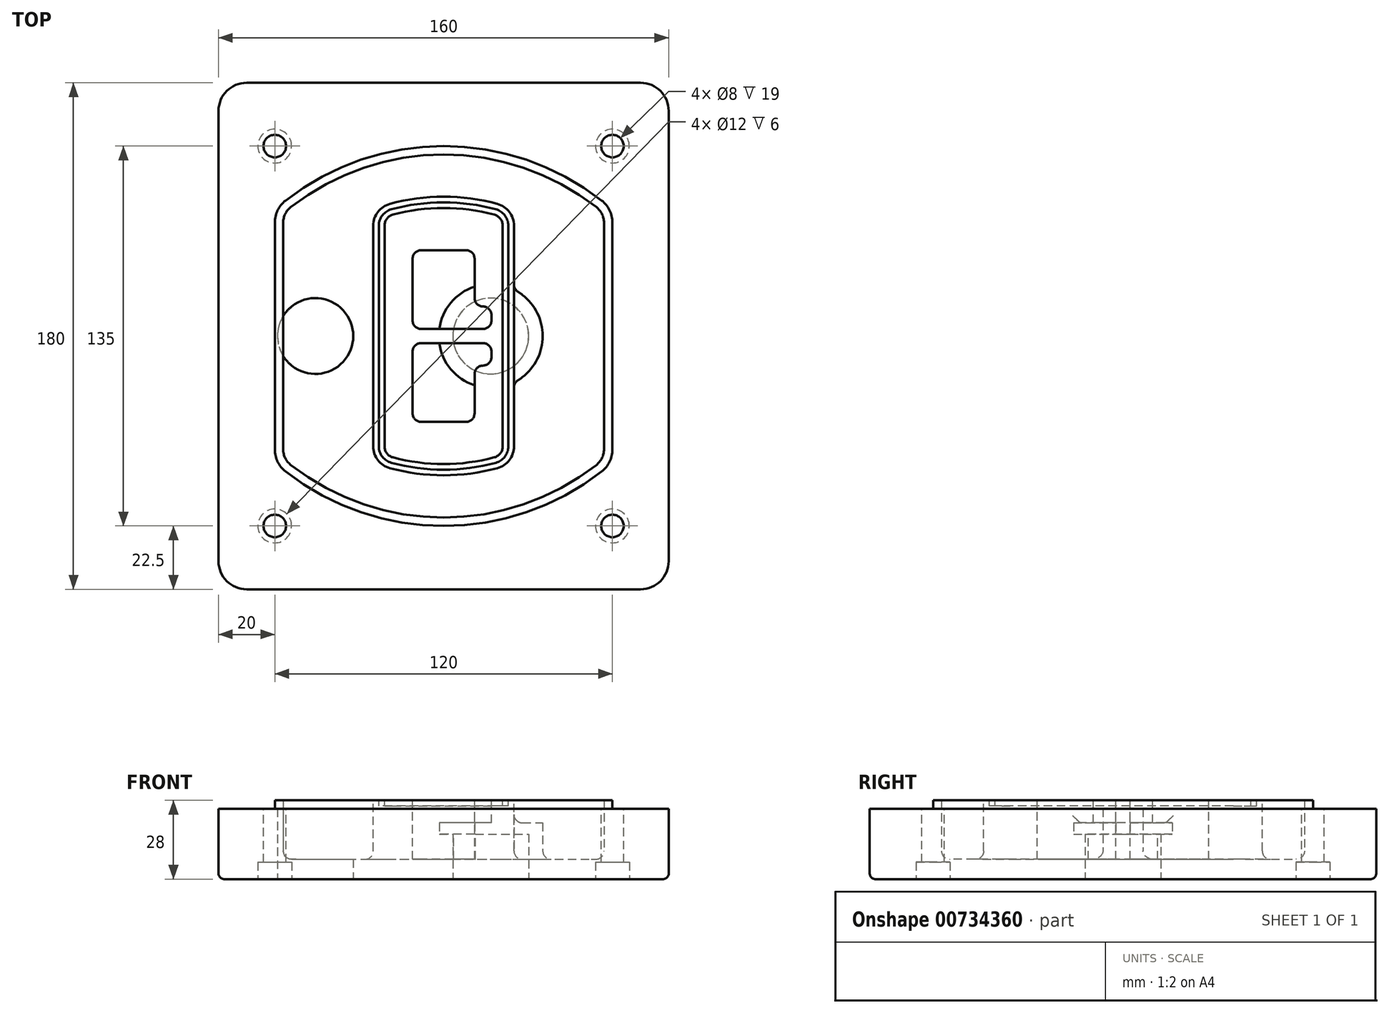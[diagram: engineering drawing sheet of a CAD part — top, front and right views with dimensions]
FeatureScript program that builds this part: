
annotation { "Feature Type Name" : "Feature", "Feature Type Description" : "" }
export const myFeature = defineFeature(function(context is Context, id is Id, definition is map)
    precondition{}
    {
        {
            var Q0;
            Q0=qCreatedBy(makeId("Top.planeOp"),FACE);
            var sketch = newSketch(context, id + "F0", { "sketchPlane" : qUnion([Q0])});
            skPoint(sketch, "E0.rect.middle", {"position": v(0, 0) * mm});
            skLineSegment(sketch, "E1.bottom", {"start": v(-70, -90) * mm, "end": v(70, -90) * mm});
            skLineSegment(sketch, "E1.top", {"start": v(-70, 90) * mm, "end": v(70, 90) * mm});
            skLineSegment(sketch, "E1.left", {"start": v(-80, -80) * mm, "end": v(-80, 80) * mm});
            skLineSegment(sketch, "E1.right", {"start": v(80, -80) * mm, "end": v(80, 80) * mm});
            skLineSegment(sketch, "E2", {"start": v(-80, 90) * mm, "end": v(80, -90) * mm, "construction": true});
            skLineSegment(sketch, "E3", {"start": v(80, 90) * mm, "end": v(-80, -90) * mm, "construction": true});
            skCircle(sketch, "E4", {"center": v(-60, 67.5) * mm, "radius": 4 * mm});
            skCircle(sketch, "E5", {"center": v(60, 67.5) * mm, "radius": 4 * mm});
            skCircle(sketch, "E6", {"center": v(60, -67.5) * mm, "radius": 4 * mm});
            skCircle(sketch, "E7", {"center": v(-60, -67.5) * mm, "radius": 4 * mm});
            skLineSegment(sketch, "E8", {"start": v(-60, 67.5) * mm, "end": v(60, 67.5) * mm, "construction": true});
            skLineSegment(sketch, "E9", {"start": v(60, 67.5) * mm, "end": v(60, -67.5) * mm, "construction": true});
            skLineSegment(sketch, "E10", {"start": v(60, -67.5) * mm, "end": v(-60, -67.5) * mm, "construction": true});
            skLineSegment(sketch, "E11", {"start": v(-60, -67.5) * mm, "end": v(-60, 67.5) * mm, "construction": true});
            skLineSegment(sketch, "E12", {"start": v(-60, 40.3) * mm, "end": v(-60, -40.3) * mm});
            skLineSegment(sketch, "E13", {"start": v(60, 40.3) * mm, "end": v(60, -40.3) * mm});
            skArc(sketch, "E14", {"start": v(56.15, 48.18) * mm, "mid": v(0, 67.5) * mm, "end": v(-56.15, 48.18) * mm});
            skArc(sketch, "E15", {"start": v(-56.15, -48.18) * mm, "mid": v(0, -67.5) * mm, "end": v(56.15, -48.18) * mm});
            skLineSegment(sketch, "E16", {"start": v(-60, 0) * mm, "end": v(60, 0) * mm, "construction": true});
            skPoint(sketch, "E17.visualSharp", {"position": v(-60, -45) * mm});
            skArc(sketch, "E17.filletArc", {"start": v(-60, -40.3) * mm, "mid": v(-58.99, -44.68) * mm, "end": v(-56.15, -48.18) * mm});
            skPoint(sketch, "E18.visualSharp", {"position": v(-60, 45) * mm});
            skArc(sketch, "E18.filletArc", {"start": v(-56.15, 48.18) * mm, "mid": v(-58.99, 44.68) * mm, "end": v(-60, 40.3) * mm});
            skPoint(sketch, "E19.visualSharp", {"position": v(60, 45) * mm});
            skArc(sketch, "E19.filletArc", {"start": v(60, 40.3) * mm, "mid": v(58.99, 44.68) * mm, "end": v(56.15, 48.18) * mm});
            skPoint(sketch, "E20.visualSharp", {"position": v(60, -45) * mm});
            skArc(sketch, "E20.filletArc", {"start": v(56.15, -48.18) * mm, "mid": v(58.99, -44.68) * mm, "end": v(60, -40.3) * mm});
            skPoint(sketch, "E21.visualSharp", {"position": v(-80, 90) * mm});
            skArc(sketch, "E21.filletArc", {"start": v(-70, 90) * mm, "mid": v(-77.07, 87.07) * mm, "end": v(-80, 80) * mm});
            skPoint(sketch, "E22.visualSharp", {"position": v(80, 90) * mm});
            skArc(sketch, "E22.filletArc", {"start": v(80, 80) * mm, "mid": v(77.07, 87.07) * mm, "end": v(70, 90) * mm});
            skPoint(sketch, "E23.visualSharp", {"position": v(80, -90) * mm});
            skArc(sketch, "E23.filletArc", {"start": v(70, -90) * mm, "mid": v(77.07, -87.07) * mm, "end": v(80, -80) * mm});
            skPoint(sketch, "E24.visualSharp", {"position": v(-80, -90) * mm});
            skArc(sketch, "E24.filletArc", {"start": v(-80, -80) * mm, "mid": v(-77.07, -87.07) * mm, "end": v(-70, -90) * mm});
            skArc(sketch, "E25.0", {"start": v(57, 40.3) * mm, "mid": v(56.3, 43.36) * mm, "end": v(54.3, 45.81) * mm});
            skLineSegment(sketch, "E25.1", {"start": v(57, 40.3) * mm, "end": v(57, -40.3) * mm});
            skArc(sketch, "E25.2", {"start": v(54.3, -45.81) * mm, "mid": v(56.3, -43.36) * mm, "end": v(57, -40.3) * mm});
            skArc(sketch, "E25.3", {"start": v(-54.3, -45.81) * mm, "mid": v(0, -64.5) * mm, "end": v(54.3, -45.81) * mm});
            skArc(sketch, "E25.4", {"start": v(-57, -40.3) * mm, "mid": v(-56.3, -43.36) * mm, "end": v(-54.3, -45.81) * mm});
            skArc(sketch, "E25.5", {"start": v(54.3, 45.81) * mm, "mid": v(0, 64.5) * mm, "end": v(-54.3, 45.81) * mm});
            skLineSegment(sketch, "E25.6", {"start": v(-57, 40.3) * mm, "end": v(-57, -40.3) * mm});
            skArc(sketch, "E25.7", {"start": v(-54.3, 45.81) * mm, "mid": v(-56.3, 43.36) * mm, "end": v(-57, 40.3) * mm});
            skArc(sketch, "E26.0", {"start": v(-58.62, 51.33) * mm, "mid": v(-62.58, 46.43) * mm, "end": v(-64, 40.3) * mm});
            skArc(sketch, "E26.1", {"start": v(58.62, 51.33) * mm, "mid": v(0, 71.5) * mm, "end": v(-58.62, 51.33) * mm});
            skArc(sketch, "E26.2", {"start": v(64, 40.3) * mm, "mid": v(62.58, 46.43) * mm, "end": v(58.62, 51.33) * mm});
            skLineSegment(sketch, "E26.3", {"start": v(64, 40.3) * mm, "end": v(64, -40.3) * mm});
            skArc(sketch, "E26.4", {"start": v(58.62, -51.33) * mm, "mid": v(62.58, -46.43) * mm, "end": v(64, -40.3) * mm});
            skLineSegment(sketch, "E26.5", {"start": v(-64, 40.3) * mm, "end": v(-64, -40.3) * mm});
            skArc(sketch, "E26.6", {"start": v(-58.62, -51.33) * mm, "mid": v(0, -71.5) * mm, "end": v(58.62, -51.33) * mm});
            skArc(sketch, "E26.7", {"start": v(-64, -40.3) * mm, "mid": v(-62.58, -46.43) * mm, "end": v(-58.62, -51.33) * mm});
            skSolve(sketch);
        }
        {
            var Q0;
            Q0=makeQuery(id+"F0.imprint","IMPRINT",FACE,{"disambiguationData":[TD([[makeQuery(id+"F0.imprint","IMPRINT",EDGE,{"derivedFrom":sQuery(id+"F0.wireOp",EDGE,"E1.bottom")}),1.0]])]});
            var Q1;
            Q1=makeQuery(id+"F0.imprint","IMPRINT",FACE,{"disambiguationData":[TD([[makeQuery(id+"F0.imprint","IMPRINT",EDGE,{"derivedFrom":sQuery(id+"F0.wireOp",EDGE,"E12")}),1.0]])]});
            var Q2;
            Q2=makeQuery(id+"F0.imprint","IMPRINT",FACE,{"disambiguationData":[TD([[makeQuery(id+"F0.imprint","IMPRINT",EDGE,{"derivedFrom":sQuery(id+"F0.wireOp",EDGE,"E25.0")}),1.0]])]});
            var Q3;
            Q3=makeQuery(id+"F0.imprint","IMPRINT",FACE,{"disambiguationData":[TD([[makeQuery(id+"F0.imprint","IMPRINT",EDGE,{"derivedFrom":sQuery(id+"F0.wireOp",EDGE,"E12")}),-1.0]])]});
            extrude(context, id + "F1", {"entities" : qUnion([Q0, Q1, Q2, Q3]), "oppositeDirection" : true, "depth" : 25 * mm, "offsetDistance" : 25 * mm});
        }
        {
            var Q0;
            Q0=makeQuery(id+"F0.imprint","IMPRINT",FACE,{"disambiguationData":[TD([[makeQuery(id+"F0.imprint","IMPRINT",EDGE,{"derivedFrom":sQuery(id+"F0.wireOp",EDGE,"E12")}),1.0]])]});
            extrude(context, id + "F2", {"entities" : qUnion([Q0]), "operationType" : NewBodyOperationType.ADD, "depth" : 3 * mm, "offsetDistance" : 25 * mm});
        }
        {
            var Q0;
            Q0=makeQuery(id+"F0.imprint","IMPRINT",FACE,{"disambiguationData":[TD([[makeQuery(id+"F0.imprint","IMPRINT",EDGE,{"derivedFrom":sQuery(id+"F0.wireOp",EDGE,"E25.0")}),1.0]])]});
            extrude(context, id + "F3", {"entities" : qUnion([Q0]), "operationType" : NewBodyOperationType.REMOVE, "oppositeDirection" : true, "depth" : 18 * mm, "offsetDistance" : 25 * mm});
        }
        {
            var Q0;
            Q0=makeQuery(id+"F2.opExtrude","CAP_FACE",FACE,{"disambiguationData":[OSD([sQuery(id+"F0.wireOp",EDGE,"E12"),sQuery(id+"F0.wireOp",EDGE,"E13"),sQuery(id+"F0.wireOp",EDGE,"E14"),sQuery(id+"F0.wireOp",EDGE,"E15"),sQuery(id+"F0.wireOp",EDGE,"E17.filletArc"),sQuery(id+"F0.wireOp",EDGE,"E18.filletArc"),sQuery(id+"F0.wireOp",EDGE,"E19.filletArc"),sQuery(id+"F0.wireOp",EDGE,"E20.filletArc"),sQuery(id+"F0.wireOp",EDGE,"E25.0"),sQuery(id+"F0.wireOp",EDGE,"E25.1"),sQuery(id+"F0.wireOp",EDGE,"E25.2"),sQuery(id+"F0.wireOp",EDGE,"E25.3"),sQuery(id+"F0.wireOp",EDGE,"E25.4"),sQuery(id+"F0.wireOp",EDGE,"E25.5"),sQuery(id+"F0.wireOp",EDGE,"E25.6"),sQuery(id+"F0.wireOp",EDGE,"E25.7")])],"isStart":false});
            var sketch = newSketch(context, id + "F4", { "sketchPlane" : qUnion([Q0])});
            skArc(sketch, "E27.0", {"start": v(-19.08, -46.97) * mm, "mid": v(0, -49.5) * mm, "end": v(19.08, -46.97) * mm});
            skArc(sketch, "E28.0", {"start": v(19.08, 46.97) * mm, "mid": v(0, 49.5) * mm, "end": v(-19.08, 46.97) * mm});
            skLineSegment(sketch, "E29", {"start": v(-25, 39.25) * mm, "end": v(-25, -39.25) * mm});
            skLineSegment(sketch, "E30", {"start": v(25, 39.25) * mm, "end": v(25, -39.25) * mm});
            skLineSegment(sketch, "E31", {"start": v(-25, 45.1) * mm, "end": v(25, 45.1) * mm, "construction": true});
            skLineSegment(sketch, "E32", {"start": v(-25, -45.1) * mm, "end": v(25, -45.1) * mm, "construction": true});
            skPoint(sketch, "E33.visualSharp", {"position": v(-25, 45.1) * mm});
            skArc(sketch, "E33.filletArc", {"start": v(-19.08, 46.97) * mm, "mid": v(-23.35, 44.11) * mm, "end": v(-25, 39.25) * mm});
            skPoint(sketch, "E34.visualSharp", {"position": v(25, 45.1) * mm});
            skArc(sketch, "E34.filletArc", {"start": v(25, 39.25) * mm, "mid": v(23.35, 44.11) * mm, "end": v(19.08, 46.97) * mm});
            skPoint(sketch, "E35.visualSharp", {"position": v(25, -45.1) * mm});
            skArc(sketch, "E35.filletArc", {"start": v(19.08, -46.97) * mm, "mid": v(23.35, -44.11) * mm, "end": v(25, -39.25) * mm});
            skPoint(sketch, "E36.visualSharp", {"position": v(-25, -45.1) * mm});
            skArc(sketch, "E36.filletArc", {"start": v(-25, -39.25) * mm, "mid": v(-23.35, -44.11) * mm, "end": v(-19.08, -46.97) * mm});
            skArc(sketch, "E37.0", {"start": v(54.3, 45.81) * mm, "mid": v(0, 64.5) * mm, "end": v(-54.3, 45.81) * mm});
            skArc(sketch, "E37.1", {"start": v(-54.3, 45.81) * mm, "mid": v(-56.3, 43.36) * mm, "end": v(-57, 40.3) * mm});
            skLineSegment(sketch, "E37.2", {"start": v(-57, 40.3) * mm, "end": v(-57, -40.3) * mm});
            skArc(sketch, "E37.3", {"start": v(-57, -40.3) * mm, "mid": v(-56.3, -43.36) * mm, "end": v(-54.3, -45.81) * mm});
            skArc(sketch, "E37.4", {"start": v(-54.3, -45.81) * mm, "mid": v(0, -64.5) * mm, "end": v(54.3, -45.81) * mm});
            skArc(sketch, "E37.5", {"start": v(54.3, -45.81) * mm, "mid": v(56.3, -43.36) * mm, "end": v(57, -40.3) * mm});
            skLineSegment(sketch, "E37.6", {"start": v(57, 40.3) * mm, "end": v(57, -40.3) * mm});
            skArc(sketch, "E37.7", {"start": v(57, 40.3) * mm, "mid": v(56.3, 43.36) * mm, "end": v(54.3, 45.81) * mm});
            skLineSegment(sketch, "E38.0", {"start": v(23, 39.25) * mm, "end": v(23, -39.25) * mm});
            skArc(sketch, "E38.1", {"start": v(18.56, -45.04) * mm, "mid": v(21.76, -42.9) * mm, "end": v(23, -39.25) * mm});
            skArc(sketch, "E38.2", {"start": v(-18.56, -45.04) * mm, "mid": v(0, -47.5) * mm, "end": v(18.56, -45.04) * mm});
            skArc(sketch, "E38.3", {"start": v(-23, -39.25) * mm, "mid": v(-21.76, -42.9) * mm, "end": v(-18.56, -45.04) * mm});
            skLineSegment(sketch, "E38.4", {"start": v(-23, 39.25) * mm, "end": v(-23, -39.25) * mm});
            skArc(sketch, "E38.5", {"start": v(23, 39.25) * mm, "mid": v(21.76, 42.9) * mm, "end": v(18.56, 45.04) * mm});
            skArc(sketch, "E38.6", {"start": v(-18.56, 45.04) * mm, "mid": v(-21.76, 42.9) * mm, "end": v(-23, 39.25) * mm});
            skArc(sketch, "E38.7", {"start": v(18.56, 45.04) * mm, "mid": v(0, 47.5) * mm, "end": v(-18.56, 45.04) * mm});
            skArc(sketch, "E39.0", {"start": v(21, 39.25) * mm, "mid": v(20.18, 41.68) * mm, "end": v(18.04, 43.1) * mm});
            skLineSegment(sketch, "E39.1", {"start": v(21, 39.25) * mm, "end": v(21, -39.25) * mm});
            skArc(sketch, "E39.2", {"start": v(18.04, -43.1) * mm, "mid": v(20.18, -41.68) * mm, "end": v(21, -39.25) * mm});
            skArc(sketch, "E39.3", {"start": v(-18.04, -43.1) * mm, "mid": v(0, -45.5) * mm, "end": v(18.04, -43.1) * mm});
            skArc(sketch, "E39.4", {"start": v(-21, -39.25) * mm, "mid": v(-20.18, -41.68) * mm, "end": v(-18.04, -43.1) * mm});
            skArc(sketch, "E39.5", {"start": v(18.04, 43.1) * mm, "mid": v(0, 45.5) * mm, "end": v(-18.04, 43.1) * mm});
            skLineSegment(sketch, "E39.6", {"start": v(-21, 39.25) * mm, "end": v(-21, -39.25) * mm});
            skArc(sketch, "E39.7", {"start": v(-18.04, 43.1) * mm, "mid": v(-20.18, 41.68) * mm, "end": v(-21, 39.25) * mm});
            skLineSegment(sketch, "E40", {"start": v(-25, 0) * mm, "end": v(25, 0) * mm, "construction": true});
            skLineSegment(sketch, "E41", {"start": v(-11, 5.5) * mm, "end": v(-11, 27.5) * mm});
            skLineSegment(sketch, "E42", {"start": v(-8, 30.5) * mm, "end": v(8, 30.5) * mm});
            skLineSegment(sketch, "E43", {"start": v(11, 27.5) * mm, "end": v(11, 13.5) * mm});
            skLineSegment(sketch, "E44", {"start": v(14, 10.5) * mm, "end": v(14, 10.5) * mm});
            skLineSegment(sketch, "E45", {"start": v(17, 7.5) * mm, "end": v(17, 5.5) * mm});
            skLineSegment(sketch, "E46", {"start": v(14, 2.5) * mm, "end": v(-8, 2.5) * mm});
            skPoint(sketch, "E47.visualSharp", {"position": v(-11, 30.5) * mm});
            skArc(sketch, "E47.filletArc", {"start": v(-8, 30.5) * mm, "mid": v(-10.12, 29.62) * mm, "end": v(-11, 27.5) * mm});
            skPoint(sketch, "E48.visualSharp", {"position": v(11, 30.5) * mm});
            skArc(sketch, "E48.filletArc", {"start": v(11, 27.5) * mm, "mid": v(10.12, 29.62) * mm, "end": v(8, 30.5) * mm});
            skPoint(sketch, "E49.visualSharp", {"position": v(11, 10.5) * mm});
            skArc(sketch, "E49.filletArc", {"start": v(11, 13.5) * mm, "mid": v(11.88, 11.38) * mm, "end": v(14, 10.5) * mm});
            skPoint(sketch, "E50.visualSharp", {"position": v(17, 10.5) * mm});
            skArc(sketch, "E50.filletArc", {"start": v(17, 7.5) * mm, "mid": v(16.12, 9.62) * mm, "end": v(14, 10.5) * mm});
            skPoint(sketch, "E51.visualSharp", {"position": v(17, 2.5) * mm});
            skArc(sketch, "E51.filletArc", {"start": v(14, 2.5) * mm, "mid": v(16.12, 3.38) * mm, "end": v(17, 5.5) * mm});
            skPoint(sketch, "E52.visualSharp", {"position": v(-11, 2.5) * mm});
            skArc(sketch, "E52.filletArc", {"start": v(-11, 5.5) * mm, "mid": v(-10.12, 3.38) * mm, "end": v(-8, 2.5) * mm});
            skLineSegment(sketch, "E53.0.MirrorCS", {"start": v(14, -2.5) * mm, "end": v(-8, -2.5) * mm});
            skArc(sketch, "E54.0.MirrorCS", {"start": v(-11, -5.5) * mm, "mid": v(-10.12, -3.38) * mm, "end": v(-8, -2.5) * mm});
            skLineSegment(sketch, "E55.0.MirrorCS", {"start": v(-11, -5.5) * mm, "end": v(-11, -27.5) * mm});
            skArc(sketch, "E56.0.MirrorCS", {"start": v(-8, -30.5) * mm, "mid": v(-10.12, -29.62) * mm, "end": v(-11, -27.5) * mm});
            skLineSegment(sketch, "E57.0.MirrorCS", {"start": v(-8, -30.5) * mm, "end": v(8, -30.5) * mm});
            skArc(sketch, "E58.0.MirrorCS", {"start": v(11, -27.5) * mm, "mid": v(10.12, -29.62) * mm, "end": v(8, -30.5) * mm});
            skLineSegment(sketch, "E59.0.MirrorCS", {"start": v(11, -27.5) * mm, "end": v(11, -13.5) * mm});
            skArc(sketch, "E60.0.MirrorCS", {"start": v(11, -13.5) * mm, "mid": v(11.88, -11.38) * mm, "end": v(14, -10.5) * mm});
            skArc(sketch, "E61.0.MirrorCS", {"start": v(17, -7.5) * mm, "mid": v(16.12, -9.62) * mm, "end": v(14, -10.5) * mm});
            skLineSegment(sketch, "E62.0.MirrorCS", {"start": v(17, -7.5) * mm, "end": v(17, -5.5) * mm});
            skArc(sketch, "E63.0.MirrorCS", {"start": v(14, -2.5) * mm, "mid": v(16.12, -3.38) * mm, "end": v(17, -5.5) * mm});
            skSolve(sketch);
        }
        {
            var Q0;
            Q0=makeQuery(id+"F4.imprint","IMPRINT",FACE,{"disambiguationData":[TD([[makeQuery(id+"F4.imprint","IMPRINT",EDGE,{"derivedFrom":sQuery(id+"F4.wireOp",EDGE,"E27.0")}),1.0]])]});
            var Q1;
            Q1=makeQuery(id+"F4.imprint","IMPRINT",FACE,{"disambiguationData":[TD([[makeQuery(id+"F4.imprint","IMPRINT",EDGE,{"derivedFrom":sQuery(id+"F4.wireOp",EDGE,"E38.0")}),-1.0]])]});
            var Q2;
            Q2=makeQuery(id+"F4.imprint","IMPRINT",FACE,{"disambiguationData":[TD([[makeQuery(id+"F4.imprint","IMPRINT",EDGE,{"derivedFrom":sQuery(id+"F4.wireOp",EDGE,"E39.0")}),1.0]])]});
            extrude(context, id + "F5", {"entities" : qUnion([Q0, Q1, Q2]), "operationType" : NewBodyOperationType.ADD, "endBound" : BoundingType.UP_TO_NEXT, "oppositeDirection" : true, "depth" : 25 * mm});
        }
        {
            var Q0;
            Q0=makeQuery(id+"F4.imprint","IMPRINT",FACE,{"disambiguationData":[TD([[makeQuery(id+"F4.imprint","IMPRINT",EDGE,{"derivedFrom":sQuery(id+"F4.wireOp",EDGE,"E38.0")}),-1.0]])]});
            extrude(context, id + "F6", {"entities" : qUnion([Q0]), "operationType" : NewBodyOperationType.REMOVE, "oppositeDirection" : true, "depth" : 2 * mm});
        }
        {
            var Q0;
            Q0=makeQuery(id+"F1.opExtrude","CAP_FACE",FACE,{"disambiguationData":[OSD([sQuery(id+"F0.wireOp",EDGE,"E1.bottom"),sQuery(id+"F0.wireOp",EDGE,"E1.top"),sQuery(id+"F0.wireOp",EDGE,"E1.left"),sQuery(id+"F0.wireOp",EDGE,"E1.right"),sQuery(id+"F0.wireOp",EDGE,"E4"),sQuery(id+"F0.wireOp",EDGE,"E5"),sQuery(id+"F0.wireOp",EDGE,"E6"),sQuery(id+"F0.wireOp",EDGE,"E7"),sQuery(id+"F0.wireOp",EDGE,"E21.filletArc"),sQuery(id+"F0.wireOp",EDGE,"E22.filletArc"),sQuery(id+"F0.wireOp",EDGE,"E23.filletArc"),sQuery(id+"F0.wireOp",EDGE,"E24.filletArc")])],"isStart":false});
            var sketch = newSketch(context, id + "F7", { "sketchPlane" : qUnion([Q0])});
            skCircle(sketch, "E64", {"center": v(16.76, 0) * mm, "radius": 13.47 * mm});
            skCircle(sketch, "E65", {"center": v(-45.56, 0) * mm, "radius": 13.47 * mm});
            skLineSegment(sketch, "E66", {"start": v(80, 0) * mm, "end": v(-80, 0) * mm});
            skCircle(sketch, "E67", {"center": v(16.76, 0) * mm, "radius": 18.47 * mm});
            skCircle(sketch, "E68", {"center": v(60, -67.5) * mm, "radius": 6 * mm});
            skCircle(sketch, "E69", {"center": v(-60, -67.5) * mm, "radius": 6 * mm});
            skCircle(sketch, "E70", {"center": v(-60, 67.5) * mm, "radius": 6 * mm});
            skCircle(sketch, "E71", {"center": v(60, 67.5) * mm, "radius": 6 * mm});
            skSolve(sketch);
        }
        {
            var Q0;
            {var subQ1=sQuery(id+"F7.wireOp",EDGE,"E66");var subQ4=sQuery(id+"F7.wireOp",EDGE,"E64");var subQ6=makeQuery(id+"F7.imprint","INTERSECT",VERTEX,{"disambiguationData":[OD(0.0)],"derivedFrom":[subQ4,subQ1]});Q0=makeQuery(id+"F7.imprint","IMPRINT",FACE,{"disambiguationData":[TD([[makeQuery(id+"F7.imprint","IMPRINT",EDGE,{"disambiguationData":[TD([[subQ6,-1.0]])],"derivedFrom":subQ4}),-1.0]])]});}
            var Q1;
            {var subQ0=sQuery(id+"F7.wireOp",EDGE,"E66");var subQ1=sQuery(id+"F7.wireOp",EDGE,"E64");var subQ3=makeQuery(id+"F7.imprint","INTERSECT",VERTEX,{"disambiguationData":[OD(0.0)],"derivedFrom":[subQ1,subQ0]});Q1=makeQuery(id+"F7.imprint","IMPRINT",FACE,{"disambiguationData":[TD([[makeQuery(id+"F7.imprint","IMPRINT",EDGE,{"disambiguationData":[TD([[subQ3,-1.0]])],"derivedFrom":subQ1}),1.0]])]});}
            var Q2;
            {var subQ0=sQuery(id+"F7.wireOp",EDGE,"E66");var subQ1=sQuery(id+"F7.wireOp",EDGE,"E64");var subQ3=makeQuery(id+"F7.imprint","INTERSECT",VERTEX,{"disambiguationData":[OD(0.0)],"derivedFrom":[subQ1,subQ0]});Q2=makeQuery(id+"F7.imprint","IMPRINT",FACE,{"disambiguationData":[TD([[makeQuery(id+"F7.imprint","IMPRINT",EDGE,{"disambiguationData":[TD([[subQ3,1.0]])],"derivedFrom":subQ1}),1.0]])]});}
            var Q3;
            {var subQ1=sQuery(id+"F7.wireOp",EDGE,"E66");var subQ4=sQuery(id+"F7.wireOp",EDGE,"E64");var subQ6=makeQuery(id+"F7.imprint","INTERSECT",VERTEX,{"disambiguationData":[OD(0.0)],"derivedFrom":[subQ4,subQ1]});Q3=makeQuery(id+"F7.imprint","IMPRINT",FACE,{"disambiguationData":[TD([[makeQuery(id+"F7.imprint","IMPRINT",EDGE,{"disambiguationData":[TD([[subQ6,1.0]])],"derivedFrom":subQ4}),-1.0]])]});}
            extrude(context, id + "F8", {"entities" : qUnion([Q0, Q1, Q2, Q3]), "operationType" : NewBodyOperationType.ADD, "oppositeDirection" : true, "depth" : 20 * mm});
        }
        {
            var Q0;
            {var subQ0=sQuery(id+"F7.wireOp",EDGE,"E66");var subQ1=sQuery(id+"F7.wireOp",EDGE,"E64");var subQ3=makeQuery(id+"F7.imprint","INTERSECT",VERTEX,{"disambiguationData":[OD(0.0)],"derivedFrom":[subQ1,subQ0]});Q0=makeQuery(id+"F7.imprint","IMPRINT",FACE,{"disambiguationData":[TD([[makeQuery(id+"F7.imprint","IMPRINT",EDGE,{"disambiguationData":[TD([[subQ3,-1.0]])],"derivedFrom":subQ1}),1.0]])]});}
            var Q1;
            {var subQ0=sQuery(id+"F7.wireOp",EDGE,"E66");var subQ1=sQuery(id+"F7.wireOp",EDGE,"E64");var subQ3=makeQuery(id+"F7.imprint","INTERSECT",VERTEX,{"disambiguationData":[OD(0.0)],"derivedFrom":[subQ1,subQ0]});Q1=makeQuery(id+"F7.imprint","IMPRINT",FACE,{"disambiguationData":[TD([[makeQuery(id+"F7.imprint","IMPRINT",EDGE,{"disambiguationData":[TD([[subQ3,1.0]])],"derivedFrom":subQ1}),1.0]])]});}
            extrude(context, id + "F9", {"entities" : qUnion([Q0, Q1]), "operationType" : NewBodyOperationType.REMOVE, "oppositeDirection" : true, "depth" : 16 * mm});
        }
        {
            var Q0;
            {var subQ0=sQuery(id+"F7.wireOp",EDGE,"E66");var subQ1=sQuery(id+"F7.wireOp",EDGE,"E65");var subQ3=makeQuery(id+"F7.imprint","INTERSECT",VERTEX,{"disambiguationData":[OD(0.0)],"derivedFrom":[subQ1,subQ0]});Q0=makeQuery(id+"F7.imprint","IMPRINT",FACE,{"disambiguationData":[TD([[makeQuery(id+"F7.imprint","IMPRINT",EDGE,{"disambiguationData":[TD([[subQ3,-1.0]])],"derivedFrom":subQ1}),1.0]])]});}
            var Q1;
            {var subQ0=sQuery(id+"F7.wireOp",EDGE,"E66");var subQ1=sQuery(id+"F7.wireOp",EDGE,"E65");var subQ3=makeQuery(id+"F7.imprint","INTERSECT",VERTEX,{"disambiguationData":[OD(0.0)],"derivedFrom":[subQ1,subQ0]});Q1=makeQuery(id+"F7.imprint","IMPRINT",FACE,{"disambiguationData":[TD([[makeQuery(id+"F7.imprint","IMPRINT",EDGE,{"disambiguationData":[TD([[subQ3,1.0]])],"derivedFrom":subQ1}),1.0]])]});}
            extrude(context, id + "F10", {"entities" : qUnion([Q0, Q1]), "operationType" : NewBodyOperationType.REMOVE, "oppositeDirection" : true, "depth" : 25 * mm});
        }
        {
            var Q0;
            Q0=makeQuery(id+"F7.imprint","IMPRINT",FACE,{"disambiguationData":[TD([[makeQuery(id+"F7.imprint","IMPRINT",EDGE,{"derivedFrom":sQuery(id+"F7.wireOp",EDGE,"E68")}),1.0]])]});
            var Q1;
            Q1=makeQuery(id+"F7.imprint","IMPRINT",FACE,{"disambiguationData":[TD([[makeQuery(id+"F7.imprint","IMPRINT",EDGE,{"derivedFrom":makeQuery(id+"F1.opExtrude","CAP_EDGE",EDGE,{"disambiguationData":[OSD([sQuery(id+"F0.wireOp",EDGE,"E5")])],"isStart":false})}),-1.0]])]});
            var Q2;
            Q2=makeQuery(id+"F7.imprint","IMPRINT",FACE,{"disambiguationData":[TD([[makeQuery(id+"F7.imprint","IMPRINT",EDGE,{"derivedFrom":sQuery(id+"F7.wireOp",EDGE,"E69")}),1.0]])]});
            var Q3;
            Q3=makeQuery(id+"F7.imprint","IMPRINT",FACE,{"disambiguationData":[TD([[makeQuery(id+"F7.imprint","IMPRINT",EDGE,{"derivedFrom":makeQuery(id+"F1.opExtrude","CAP_EDGE",EDGE,{"disambiguationData":[OSD([sQuery(id+"F0.wireOp",EDGE,"E4")])],"isStart":false})}),-1.0]])]});
            var Q4;
            Q4=makeQuery(id+"F7.imprint","IMPRINT",FACE,{"disambiguationData":[TD([[makeQuery(id+"F7.imprint","IMPRINT",EDGE,{"derivedFrom":sQuery(id+"F7.wireOp",EDGE,"E70")}),1.0]])]});
            var Q5;
            Q5=makeQuery(id+"F7.imprint","IMPRINT",FACE,{"disambiguationData":[TD([[makeQuery(id+"F7.imprint","IMPRINT",EDGE,{"derivedFrom":makeQuery(id+"F1.opExtrude","CAP_EDGE",EDGE,{"disambiguationData":[OSD([sQuery(id+"F0.wireOp",EDGE,"E7")])],"isStart":false})}),-1.0]])]});
            var Q6;
            Q6=makeQuery(id+"F7.imprint","IMPRINT",FACE,{"disambiguationData":[TD([[makeQuery(id+"F7.imprint","IMPRINT",EDGE,{"derivedFrom":sQuery(id+"F7.wireOp",EDGE,"E71")}),1.0]])]});
            var Q7;
            Q7=makeQuery(id+"F7.imprint","IMPRINT",FACE,{"disambiguationData":[TD([[makeQuery(id+"F7.imprint","IMPRINT",EDGE,{"derivedFrom":makeQuery(id+"F1.opExtrude","CAP_EDGE",EDGE,{"disambiguationData":[OSD([sQuery(id+"F0.wireOp",EDGE,"E6")])],"isStart":false})}),-1.0]])]});
            extrude(context, id + "F11", {"entities" : qUnion([Q0, Q1, Q2, Q3, Q4, Q5, Q6, Q7]), "operationType" : NewBodyOperationType.REMOVE, "oppositeDirection" : true, "depth" : 6 * mm});
        }
        {
            var Q0;
            Q0=makeQuery(id+"F9.boolean.opBoolean","COPY",FACE,{"derivedFrom":makeQuery(id+"F9.opExtrude","CAP_FACE",FACE,{"disambiguationData":[OSD([sQuery(id+"F7.wireOp",EDGE,"E64")])],"isStart":false})});
            var sketch = newSketch(context, id + "F12", { "sketchPlane" : qUnion([Q0])});
            skArc(sketch, "E72.0", {"start": v(11, 17.55) * mm, "mid": v(2.57, 11.82) * mm, "end": v(-1.54, 2.5) * mm});
            skArc(sketch, "E72.1", {"start": v(-1.54, -2.5) * mm, "mid": v(2.57, -11.82) * mm, "end": v(11, -17.55) * mm});
            skLineSegment(sketch, "E73", {"start": v(-1.54, -2.5) * mm, "end": v(14, -2.5) * mm});
            skLineSegment(sketch, "E74.0", {"start": v(14, 2.5) * mm, "end": v(-1.54, 2.5) * mm});
            skArc(sketch, "E74.1", {"start": v(14, 2.5) * mm, "mid": v(16.12, 3.38) * mm, "end": v(17, 5.5) * mm});
            skLineSegment(sketch, "E74.2", {"start": v(17, 7.5) * mm, "end": v(17, 5.5) * mm});
            skArc(sketch, "E74.3", {"start": v(17, 7.5) * mm, "mid": v(16.12, 9.62) * mm, "end": v(14, 10.5) * mm});
            skArc(sketch, "E74.4", {"start": v(11, 13.5) * mm, "mid": v(11.88, 11.38) * mm, "end": v(14, 10.5) * mm});
            skLineSegment(sketch, "E74.5", {"start": v(11, 17.55) * mm, "end": v(11, 13.5) * mm});
            skLineSegment(sketch, "E74.7", {"start": v(14, -2.5) * mm, "end": v(-1.54, -2.5) * mm});
            skArc(sketch, "E74.8", {"start": v(14, -2.5) * mm, "mid": v(16.12, -3.38) * mm, "end": v(17, -5.5) * mm});
            skLineSegment(sketch, "E74.9", {"start": v(17, -7.5) * mm, "end": v(17, -5.5) * mm});
            skArc(sketch, "E74.10", {"start": v(17, -7.5) * mm, "mid": v(16.12, -9.62) * mm, "end": v(14, -10.5) * mm});
            skArc(sketch, "E74.11", {"start": v(11, -13.5) * mm, "mid": v(11.88, -11.38) * mm, "end": v(14, -10.5) * mm});
            skLineSegment(sketch, "E74.12", {"start": v(11, -17.55) * mm, "end": v(11, -13.5) * mm});
            skPoint(sketch, "E75.orphan", {"position": v(11, -27.5) * mm});
            skPoint(sketch, "E76.orphan", {"position": v(-8, -2.5) * mm});
            skPoint(sketch, "E77.orphan", {"position": v(-8, 2.5) * mm});
            skPoint(sketch, "E78.orphan", {"position": v(11, 27.5) * mm});
            skSolve(sketch);
        }
        {
            var Q0;
            {var subQ7=sQuery(id+"F12.wireOp",EDGE,"E72.0");var subQ14=sQuery(id+"F12.wireOp",EDGE,"E72.1");var subQ16=sQuery(id+"F12.wireOp",EDGE,"E74.1");var subQ18=sQuery(id+"F12.wireOp",EDGE,"E74.8");Q0=qUnion([makeQuery(id+"F12.imprint","IMPRINT",FACE,{"disambiguationData":[TD([[makeQuery(id+"F12.imprint","IMPRINT",EDGE,{"derivedFrom":subQ7}),1.0]])]}),makeQuery(id+"F12.imprint","IMPRINT",FACE,{"disambiguationData":[TD([[makeQuery(id+"F12.imprint","IMPRINT",EDGE,{"derivedFrom":subQ14}),1.0]])]}),makeQuery(id+"F12.imprint","IMPRINT",FACE,{"disambiguationData":[TD([[makeQuery(id+"F12.imprint","IMPRINT",EDGE,{"derivedFrom":subQ16}),1.0]])]}),makeQuery(id+"F12.imprint","IMPRINT",FACE,{"disambiguationData":[TD([[makeQuery(id+"F12.imprint","IMPRINT",EDGE,{"derivedFrom":subQ18}),-1.0]])]})]);}
            var Q1;
            Q1=makeQuery(id+"F5.boolean.opBoolean","SPLIT",FACE,{"disambiguationData":[TD([makeQuery(id+"F5.opExtrude","SWEPT_FACE",FACE,{"disambiguationData":[OSD([sQuery(id+"F4.wireOp",EDGE,"E41")])]})])],"derivedFrom":makeQuery(id+"F3.boolean.opBoolean","COPY",FACE,{"derivedFrom":makeQuery(id+"F3.opExtrude","CAP_FACE",FACE,{"disambiguationData":[OSD([sQuery(id+"F0.wireOp",EDGE,"E25.0"),sQuery(id+"F0.wireOp",EDGE,"E25.1"),sQuery(id+"F0.wireOp",EDGE,"E25.2"),sQuery(id+"F0.wireOp",EDGE,"E25.3"),sQuery(id+"F0.wireOp",EDGE,"E25.4"),sQuery(id+"F0.wireOp",EDGE,"E25.5"),sQuery(id+"F0.wireOp",EDGE,"E25.6"),sQuery(id+"F0.wireOp",EDGE,"E25.7")])],"isStart":false})})});
            extrude(context, id + "F13", {"entities" : qUnion([Q0]), "operationType" : NewBodyOperationType.REMOVE, "endBound" : BoundingType.UP_TO_SURFACE, "endBoundEntityFace" : qUnion([Q1]), "depth" : 25 * mm});
        }
        {
            var Q0;
            Q0=makeQuery(id+"F3.boolean.opBoolean","COPY",EDGE,{"derivedFrom":makeQuery(id+"F3.opExtrude","CAP_EDGE",EDGE,{"disambiguationData":[OSD([sQuery(id+"F0.wireOp",EDGE,"E25.6")])],"isStart":false})});
            var Q1;
            Q1=makeQuery(id+"F8.boolean.opBoolean","INTERSECT",EDGE,{"derivedFrom":[makeQuery(id+"F5.opExtrude","SWEPT_FACE",FACE,{"disambiguationData":[OSD([sQuery(id+"F4.wireOp",EDGE,"E30")])]}),makeQuery(id+"F8.opExtrude","CAP_FACE",FACE,{"disambiguationData":[OSD([sQuery(id+"F7.wireOp",EDGE,"E67")])],"isStart":false})]});
            var Q2;
            Q2=makeQuery(id+"F8.boolean.opBoolean","INTERSECT",EDGE,{"disambiguationData":[OD(1.0)],"derivedFrom":[makeQuery(id+"F5.opExtrude","SWEPT_FACE",FACE,{"disambiguationData":[OSD([sQuery(id+"F4.wireOp",EDGE,"E30")])]}),makeQuery(id+"F8.opExtrude","SWEPT_FACE",FACE,{"disambiguationData":[OSD([sQuery(id+"F7.wireOp",EDGE,"E67")])]})]});
            var Q3;
            {var subQ0=sQuery(id+"F4.wireOp",EDGE,"E30");Q3=makeQuery(id+"F8.boolean.opBoolean","SPLIT",EDGE,{"disambiguationData":[TD([makeQuery(id+"F5.opExtrude","SWEPT_FACE",FACE,{"disambiguationData":[OSD([sQuery(id+"F4.wireOp",EDGE,"E35.filletArc")])]})])],"derivedFrom":makeQuery(id+"F5.opExtrude","CAP_EDGE",EDGE,{"disambiguationData":[OSD([subQ0])],"isStart":false})});}
            var Q4;
            {var subQ0=sQuery(id+"F0.wireOp",EDGE,"E25.7");var subQ1=sQuery(id+"F0.wireOp",EDGE,"E25.1");var subQ2=sQuery(id+"F0.wireOp",EDGE,"E25.6");var subQ3=sQuery(id+"F0.wireOp",EDGE,"E25.5");var subQ4=sQuery(id+"F0.wireOp",EDGE,"E25.4");var subQ5=sQuery(id+"F0.wireOp",EDGE,"E25.0");var subQ6=sQuery(id+"F0.wireOp",EDGE,"E25.2");var subQ7=sQuery(id+"F0.wireOp",EDGE,"E25.3");Q4=makeQuery(id+"F8.boolean.opBoolean","INTERSECT",EDGE,{"derivedFrom":[makeQuery(id+"F5.boolean.opBoolean","SPLIT",FACE,{"disambiguationData":[TD([makeQuery(id+"F2.opExtrude","SWEPT_FACE",FACE,{"disambiguationData":[OSD([subQ5])]})])],"derivedFrom":makeQuery(id+"F3.boolean.opBoolean","COPY",FACE,{"derivedFrom":makeQuery(id+"F3.opExtrude","CAP_FACE",FACE,{"disambiguationData":[OSD([subQ5,subQ1,subQ6,subQ7,subQ4,subQ3,subQ2,subQ0])],"isStart":false})})}),makeQuery(id+"F8.opExtrude","SWEPT_FACE",FACE,{"disambiguationData":[OSD([sQuery(id+"F7.wireOp",EDGE,"E67")])]})]});}
            var Q5;
            Q5=makeQuery(id+"F8.boolean.opBoolean","INTERSECT",EDGE,{"disambiguationData":[OD(0.0)],"derivedFrom":[makeQuery(id+"F5.opExtrude","SWEPT_FACE",FACE,{"disambiguationData":[OSD([sQuery(id+"F4.wireOp",EDGE,"E30")])]}),makeQuery(id+"F8.opExtrude","SWEPT_FACE",FACE,{"disambiguationData":[OSD([sQuery(id+"F7.wireOp",EDGE,"E67")])]})]});
            fillet(context, id + "F14", {"entities" : qUnion([Q0, Q1, Q2, Q3, Q4, Q5]), "radius" : 3 * mm, "tangentPropagation" : true, "allowEdgeOverflow" : false});
        }
        {
            var Q0;
            Q0=makeQuery(id+"F1.opExtrude","CAP_EDGE",EDGE,{"disambiguationData":[OSD([sQuery(id+"F0.wireOp",EDGE,"E1.bottom")])],"isStart":false});
            fillet(context, id + "F15", {"entities" : qUnion([Q0]), "radius" : 2 * mm, "tangentPropagation" : true, "allowEdgeOverflow" : false});
        }
    });
